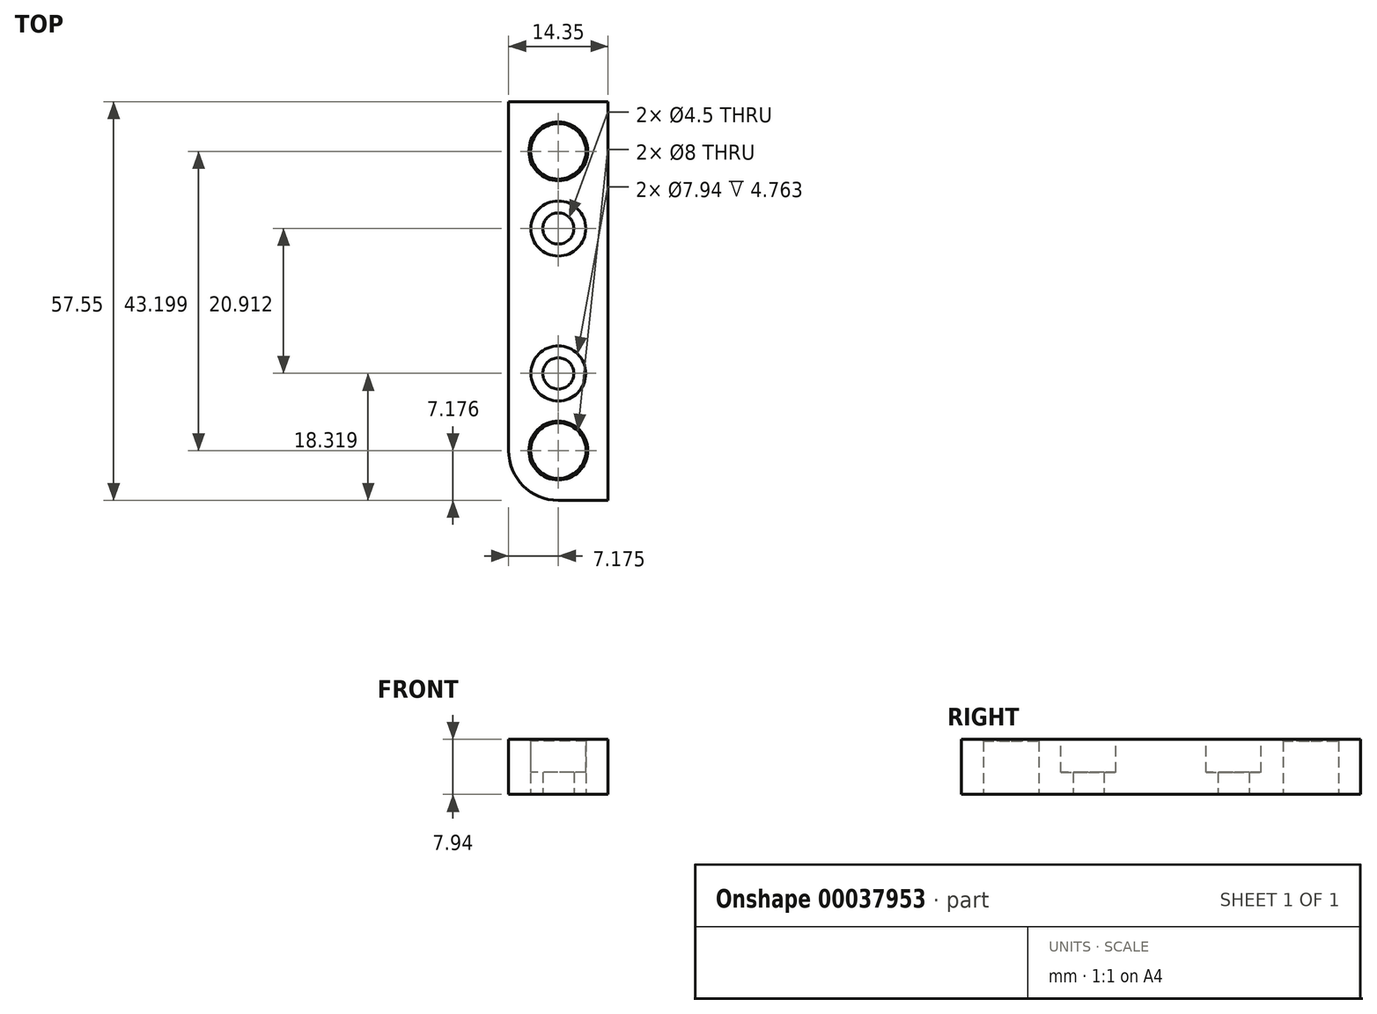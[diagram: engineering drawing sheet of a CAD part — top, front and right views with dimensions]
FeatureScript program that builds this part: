
annotation { "Feature Type Name" : "Feature", "Feature Type Description" : "" }
export const myFeature = defineFeature(function(context is Context, id is Id, definition is map)
    precondition{}
    {
        {
            var Q0;
            Q0=qCreatedBy(makeId("Top.planeOp"),FACE);
            var sketch = newSketch(context, id + "F0", { "sketchPlane" : qUnion([Q0])});
            skLineSegment(sketch, "E0.bottom", {"start": v(0, 0) * mm, "end": v(-14.35, 0) * mm});
            skLineSegment(sketch, "E0.top", {"start": v(0, -57.55) * mm, "end": v(-14.35, -57.55) * mm});
            skLineSegment(sketch, "E0.left", {"start": v(0, 0) * mm, "end": v(0, -57.55) * mm});
            skLineSegment(sketch, "E0.right", {"start": v(-14.35, 0) * mm, "end": v(-14.35, -57.55) * mm});
            skLineSegment(sketch, "E1", {"start": v(-7.18, 0) * mm, "end": v(-7.18, -7.18) * mm, "construction": true});
            skLineSegment(sketch, "E2", {"start": v(-7.18, -57.55) * mm, "end": v(-7.18, -50.37) * mm, "construction": true});
            skCircle(sketch, "E3", {"center": v(-7.18, -7.18) * mm, "radius": 4 * mm});
            skCircle(sketch, "E4", {"center": v(-7.18, -50.37) * mm, "radius": 4 * mm});
            skLineSegment(sketch, "E5", {"start": v(-7.18, -7.18) * mm, "end": v(-7.18, -18.32) * mm, "construction": true});
            skLineSegment(sketch, "E6", {"start": v(-7.18, -50.37) * mm, "end": v(-7.18, -39.23) * mm, "construction": true});
            skCircle(sketch, "E7", {"center": v(-7.18, -18.32) * mm, "radius": 2.25 * mm});
            skCircle(sketch, "E8", {"center": v(-7.18, -39.23) * mm, "radius": 2.25 * mm});
            skSolve(sketch);
        }
        {
            var Q0;
            Q0=qSketchRegion(id+"F0",true);
            extrude(context, id + "F1", {"entities" : qUnion([Q0]), "depth" : 7.94 * mm});
        }
        {
            var Q0;
            Q0=makeQuery(id+"F1.opExtrude","CAP_FACE",FACE,{"disambiguationData":[OSD([sQuery(id+"F0.wireOp",EDGE,"E0.bottom"),sQuery(id+"F0.wireOp",EDGE,"E0.top"),sQuery(id+"F0.wireOp",EDGE,"E0.left"),sQuery(id+"F0.wireOp",EDGE,"E0.right"),sQuery(id+"F0.wireOp",EDGE,"E3"),sQuery(id+"F0.wireOp",EDGE,"E4"),sQuery(id+"F0.wireOp",EDGE,"E7"),sQuery(id+"F0.wireOp",EDGE,"E8"),sQuery(id+"F0.wireOp",EDGE,"cdc09b9e-eba4-401b-a8ed-d77c5918dbf7.rect.bottom"),sQuery(id+"F0.wireOp",EDGE,"cdc09b9e-eba4-401b-a8ed-d77c5918dbf7.rect.top"),sQuery(id+"F0.wireOp",EDGE,"cdc09b9e-eba4-401b-a8ed-d77c5918dbf7.rect.left"),sQuery(id+"F0.wireOp",EDGE,"cdc09b9e-eba4-401b-a8ed-d77c5918dbf7.rect.right")])],"isStart":false});
            var sketch = newSketch(context, id + "F2", { "sketchPlane" : qUnion([Q0])});
            skCircle(sketch, "E9", {"center": v(-7.18, -18.32) * mm, "radius": 3.97 * mm});
            skCircle(sketch, "E10", {"center": v(-7.18, -39.23) * mm, "radius": 3.97 * mm});
            skSolve(sketch);
        }
        {
            var Q0;
            Q0=qSketchRegion(id+"F2",true);
            extrude(context, id + "F3", {"entities" : qUnion([Q0]), "operationType" : NewBodyOperationType.REMOVE, "oppositeDirection" : true, "depth" : 4.76 * mm});
        }
        {
            var Q0;
            Q0=makeQuery(id+"F1.opExtrude","CAP_EDGE",EDGE,{"disambiguationData":[OSD([sQuery(id+"F0.wireOp",EDGE,"E3")])],"isStart":false});
            var Q1;
            Q1=makeQuery(id+"F1.opExtrude","CAP_EDGE",EDGE,{"disambiguationData":[OSD([sQuery(id+"F0.wireOp",EDGE,"E4")])],"isStart":false});
            chamfer(context, id + "F4", {"entities" : qUnion([Q0, Q1]), "width" : 0.25 * mm, "tangentPropagation" : true});
        }
        {
            var Q0;
            Q0=makeQuery(id+"F1.opExtrude","SWEPT_EDGE",EDGE,{"disambiguationData":[OSD([sQuery(id+"F0.wireOp",EDGE,"E0.top"),sQuery(id+"F0.wireOp",EDGE,"E0.right")])]});
            fillet(context, id + "F5", {"entities" : qUnion([Q0]), "radius" : 7.18 * mm, "tangentPropagation" : true, "allowEdgeOverflow" : false});
        }
    });
